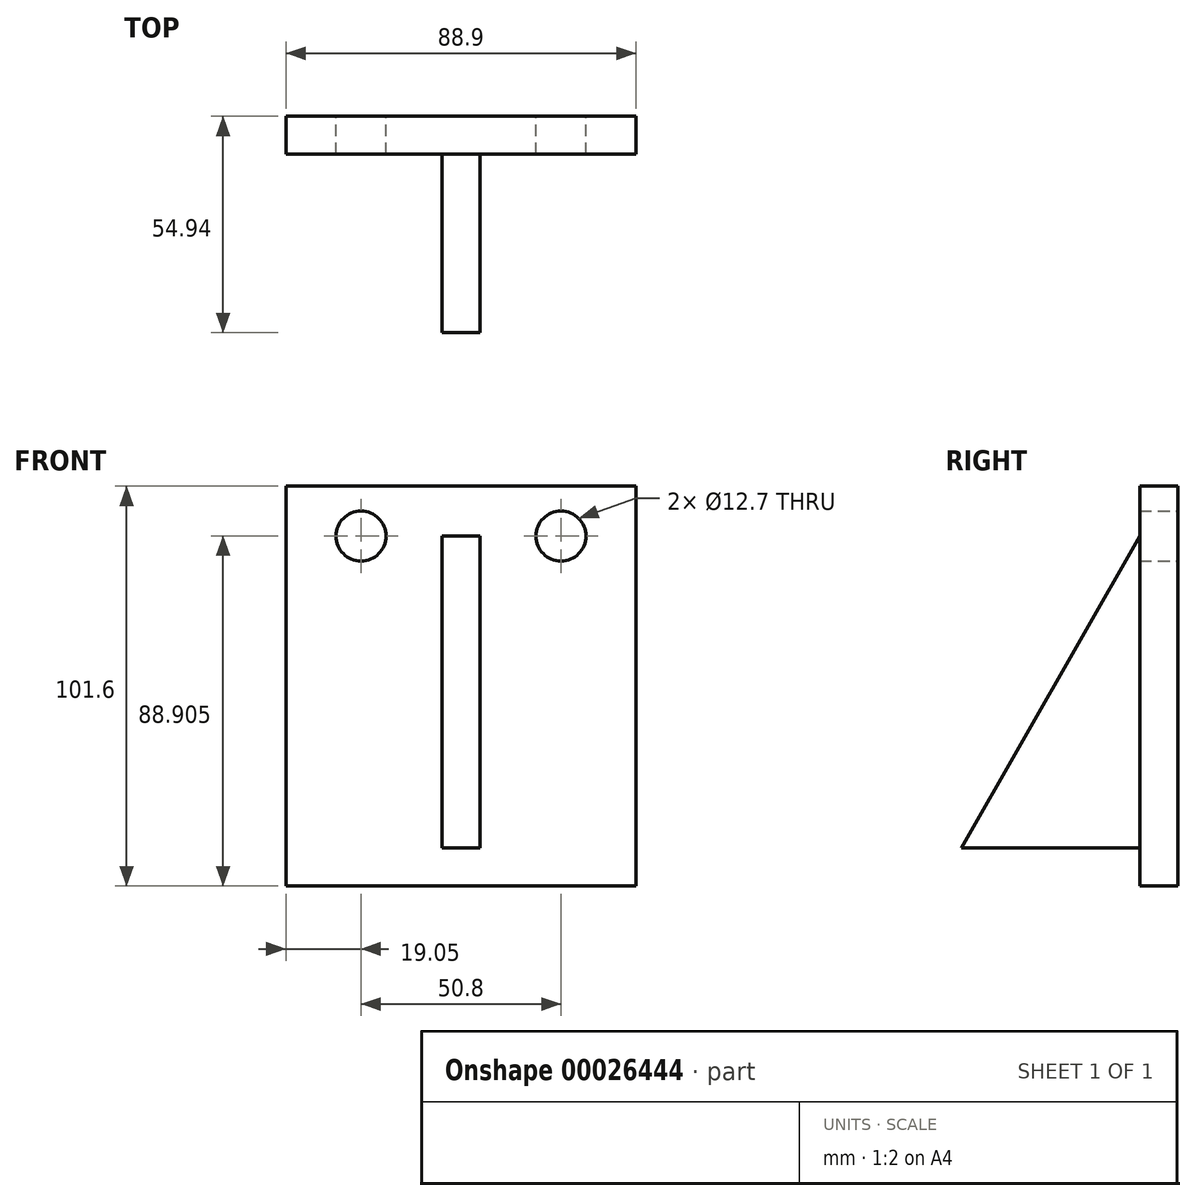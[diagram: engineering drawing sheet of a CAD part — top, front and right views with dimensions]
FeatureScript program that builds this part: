
annotation { "Feature Type Name" : "Feature", "Feature Type Description" : "" }
export const myFeature = defineFeature(function(context is Context, id is Id, definition is map)
    precondition{}
    {
        {
            var Q0;
            Q0=qCreatedBy(makeId("Front.planeOp"),FACE);
            var sketch = newSketch(context, id + "F0", { "sketchPlane" : qUnion([Q0])});
            skLineSegment(sketch, "E0.bottom", {"start": v(-65.39, 47.98) * mm, "end": v(23.51, 47.98) * mm});
            skLineSegment(sketch, "E0.top", {"start": v(-65.39, -53.62) * mm, "end": v(23.51, -53.62) * mm});
            skLineSegment(sketch, "E0.left", {"start": v(-65.39, 47.98) * mm, "end": v(-65.39, -53.62) * mm});
            skLineSegment(sketch, "E0.right", {"start": v(23.51, 47.98) * mm, "end": v(23.51, -53.62) * mm});
            skLineSegment(sketch, "E1.0", {"start": v(-25.77, 35.28) * mm, "end": v(-16.11, 35.28) * mm});
            skCircle(sketch, "E2", {"center": v(-46.34, 35.28) * mm, "radius": 6.35 * mm});
            skCircle(sketch, "E3", {"center": v(4.46, 35.28) * mm, "radius": 6.35 * mm});
            skLineSegment(sketch, "E4.0", {"start": v(-25.77, 35.28) * mm, "end": v(-25.77, -53.62) * mm});
            skLineSegment(sketch, "E5.0", {"start": v(-16.11, 35.28) * mm, "end": v(-16.11, -53.62) * mm});
            skLineSegment(sketch, "E6", {"start": v(-25.77, -53.62) * mm, "end": v(-16.11, -53.62) * mm});
            skSolve(sketch);
        }
        {
            var Q0;
            Q0=makeQuery(id+"F0.imprint","IMPRINT",FACE,{"disambiguationData":[TD([[makeQuery(id+"F0.imprint","IMPRINT",EDGE,{"derivedFrom":sQuery(id+"F0.wireOp",EDGE,"E1.0")}),-1.0]])]});
            extrude(context, id + "F1", {"entities" : qUnion([Q0]), "depth" : 50.8 * mm});
        }
        {
            var Q0;
            Q0 = qSketchRegion(id + "F0", true);
            var Q1;
            Q1=makeQuery(id+"F1.opExtrude","CAP_FACE",FACE,{"disambiguationData":[OSD([sQuery(id+"F0.wireOp",EDGE,"E1.0"),sQuery(id+"F0.wireOp",EDGE,"E4.0"),sQuery(id+"F0.wireOp",EDGE,"E5.0"),sQuery(id+"F0.wireOp",EDGE,"E6")])],"isStart":false});
            extrude(context, id + "F2", {"entities" : qUnion([Q0, Q1]), "operationType" : NewBodyOperationType.ADD, "depth" : 9.65 * mm});
        }
        {
            var Q0;
            {var subQ0=sQuery(id+"F0.wireOp",EDGE,"E5.0");Q0=makeQuery(id+"F2.boolean.opBoolean","MERGE",FACE,{"derivedFrom":[makeQuery(id+"F1.opExtrude","SWEPT_FACE",FACE,{"disambiguationData":[OSD([subQ0])]}),makeQuery(id+"F2.opExtrude","SWEPT_FACE",FACE,{"disambiguationData":[OSD([subQ0])]})]});}
            var sketch = newSketch(context, id + "F3", { "sketchPlane" : qUnion([Q0])});
            skLineSegment(sketch, "E7", {"start": v(-9.65, 35.28) * mm, "end": v(-60.45, -53.62) * mm});
            skLineSegment(sketch, "E8", {"start": v(-9.65, 35.28) * mm, "end": v(-60.45, 35.28) * mm});
            skLineSegment(sketch, "E9", {"start": v(-60.45, 35.28) * mm, "end": v(-60.45, -53.62) * mm});
            skSolve(sketch);
        }
        {
            var Q0;
            Q0=makeQuery(id+"F3.imprint","IMPRINT",FACE,{"disambiguationData":[TD([[makeQuery(id+"F3.imprint","IMPRINT",EDGE,{"derivedFrom":sQuery(id+"F3.wireOp",EDGE,"E7")}),-1.0]])]});
            extrude(context, id + "F4", {"entities" : qUnion([Q0]), "operationType" : NewBodyOperationType.REMOVE, "endBound" : BoundingType.THROUGH_ALL, "oppositeDirection" : true, "depth" : 25.4 * mm});
        }
        {
            var Q0;
            {var subQ0=sQuery(id+"F0.wireOp",EDGE,"E5.0");Q0=makeQuery(id+"F2.boolean.opBoolean","MERGE",FACE,{"derivedFrom":[makeQuery(id+"F1.opExtrude","SWEPT_FACE",FACE,{"disambiguationData":[OSD([subQ0])]}),makeQuery(id+"F2.opExtrude","SWEPT_FACE",FACE,{"disambiguationData":[OSD([subQ0])]})]});}
            var sketch = newSketch(context, id + "F5", { "sketchPlane" : qUnion([Q0])});
            skLineSegment(sketch, "E10.0", {"start": v(-54.94, -43.96) * mm, "end": v(-9.65, -43.96) * mm});
            skLineSegment(sketch, "E11", {"start": v(-54.94, -43.96) * mm, "end": v(-60.45, -53.62) * mm});
            skLineSegment(sketch, "E12", {"start": v(-60.45, -53.62) * mm, "end": v(-9.65, -53.62) * mm});
            skLineSegment(sketch, "E13", {"start": v(-9.65, -53.62) * mm, "end": v(-9.65, -43.96) * mm});
            skSolve(sketch);
        }
        {
            var Q0;
            Q0=makeQuery(id+"F5.imprint","IMPRINT",FACE,{"disambiguationData":[TD([[makeQuery(id+"F5.imprint","IMPRINT",EDGE,{"derivedFrom":sQuery(id+"F5.wireOp",EDGE,"E10.0")}),-1.0]])]});
            extrude(context, id + "F6", {"entities" : qUnion([Q0]), "operationType" : NewBodyOperationType.REMOVE, "endBound" : BoundingType.THROUGH_ALL, "oppositeDirection" : true, "depth" : 25.4 * mm});
        }
    });
